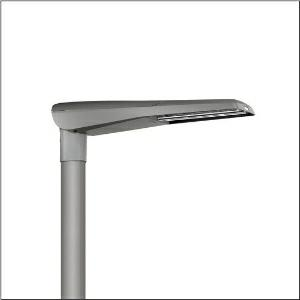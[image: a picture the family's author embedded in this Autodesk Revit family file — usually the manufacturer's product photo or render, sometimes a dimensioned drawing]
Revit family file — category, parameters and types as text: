
# Revit family: streetlight_sl_11_iq_mini___st1_0ab_5xc2nc1f08he_e776
name_source: partatom
category: Lighting Fixtures
units: mm (PartAtom-declared; Revit-internal decimal feet)

## family parameters
Cut with Voids When Loaded = No
Host = Face
Light Source = No
Part Type = Normal
Room Calculation Point = No
Round Connector Dimension = Use Diameter
Shared = No

## types (1)
- --- (1 x LED, 5460 lm, 63.6 W, 2200K)
    Apparent Load = 64 VA
    CIE Flux Codes = 29 63 95 100 100
    Color Rendering = 70
    Color Temperature = 2200K
    Default Elevation = 1800 mm
    Description = Streetlight SL 11 iQ mini, mast luminaire, primary light control with 3 zone facetted reflector, of plastic, silver coated, highly specular, primary optical cover: cover, of PMMA, transparent, light distribution: ST1.0aB, light emission: direct distribution, primary light characteristic: asymmetric, installation type: post-top, side-entry, LED, High Power LED, rated luminous flux: 7.020lm, luminous efficacy: 113lm/W, light colour: 722/727/730/740, colour temperature: 2200/2700/3000/4000K, control gear: iQ Street-Remote, control: Street-Remote, Auto-Match, Temp-Guard, Lumen-Switch, Night-Set, Smart-Wire, Light-Fading, Desk-Remote (wireless, voltage-free reading and setting of iQ features in the workshop via application-optimized NFC function/RFID function), optimised constant luminous flux control (CLO 2.0), with cable H07RN-F 5x 1.5mm², mains connection: 230..240V, AC, 50/60Hz, connection cable pre-assembled, cable length: 8,5m, start of lifetime: 62W, end of service life: 66W, reduction: 29W, luminaire housing, of diecast aluminium, powder-coated, Siteco® metallic grey (DB 702S), please order mast flange separately, inclination adjustable without tools: 0°, 5°, 10°, 15° (post-top) | 0°, -5°, -10°, -15° (side-entry), sealing non-destructively replaceable, multi-level sealing system, length: 736mm, width: 174mm, height: 116mm, mast flange for spigot size: 42mm (side-entry): 5XC10008XM4, 60/48mm (side-entry/post-top): 5XC10108XM2, 76/60mm (side-entry/post-top): 5XC10108XM1, mounting height: 4..8m, equipment: Power, protection rating (complete): IP66, insulation class (complete): insulation class II (safety insulation), certification: CE, ENEC, VDE, impact resistance: IK09, permissible operating ambient temperature for outdoor applications: -25..+50°C, standard-compliant lighting for roads and squares, Environmental Product Declaration (EPD) tested and certified by an independent institute, packaging unit: 1 piece

Light Distribution: ST1.0aB
    Height = 116 mm
    Lamp = 1 x LED
    Lamp Light Flux = 5460 lm
    Lamp Power = 63.6 W
    Lamp count = 1
    Length = 736 mm
    Luminous efficacy = 86 lm/W
    Manufacturer = Siteco
    ModVariant = No
    Model = 5XC2NC1F08HE
    Number of Poles = 1
    OnlyDefault = Yes
    Power Factor = 1
    Product Name = Streetlight SL 11 iQ mini | ST1.0aB
    Product group = mast luminaire | pylon top
    ProductGroupID = 6100
    Protection Class = Protection class II
    Protection Degree = IP 66
    RLX_Detail_Level = 1
    RLX_Emergency_Light_Flux = 0 lm
    RLX_Emergency_Type = 0
    RLX_Emergency_Type_DB = No
    RlxData = <blob elided: 34885 chars, md5=11057d7b>
    Socket = socket
    Standby Power = 0 W
    System Light Flux = 5460 lm
    System Power = 64 W
    Type Comments = individual setting: luminous flux: 100 % | dim-lin: 254 | 866 mA
    Type Image = l_1003508.jpg
    URL = http://relux.com
    VarID = @adj_001407
    Voltage = 0 V
    Weight = 0.00 kg
    Width = 174 mm

## geometry (parser evidence)
native form markers: Blend x4, Sweep x10
no freeform markers — native parametric forms only
